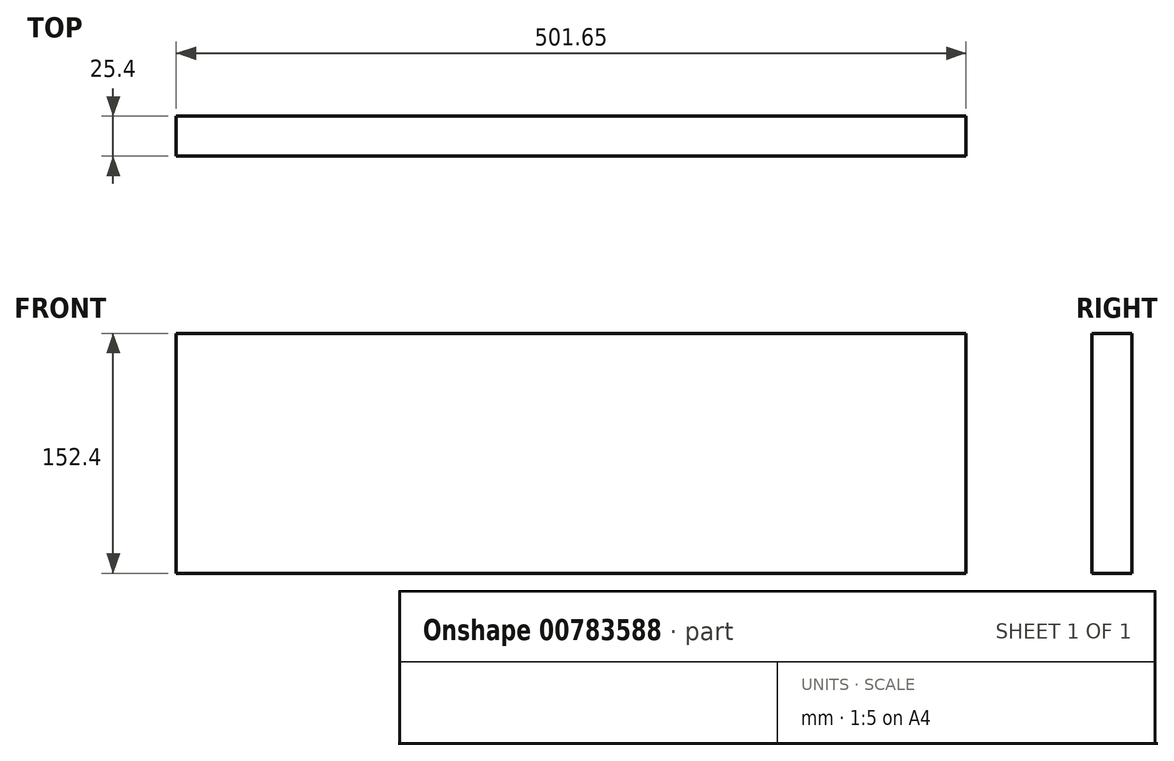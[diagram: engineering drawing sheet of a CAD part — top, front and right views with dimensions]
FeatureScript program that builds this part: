
annotation { "Feature Type Name" : "Feature", "Feature Type Description" : "" }
export const myFeature = defineFeature(function(context is Context, id is Id, definition is map)
    precondition{}
    {
        {
            var Q0;
            Q0=qCreatedBy(makeId("Front.planeOp"),FACE);
            var sketch = newSketch(context, id + "F0", { "sketchPlane" : qUnion([Q0])});
            skLineSegment(sketch, "E0.bottom", {"start": v(0, 0) * mm, "end": v(501.65, 0) * mm});
            skLineSegment(sketch, "E0.top", {"start": v(0, 152.4) * mm, "end": v(501.65, 152.4) * mm});
            skLineSegment(sketch, "E0.left", {"start": v(0, 0) * mm, "end": v(0, 152.4) * mm});
            skLineSegment(sketch, "E0.right", {"start": v(501.65, 0) * mm, "end": v(501.65, 152.4) * mm});
            skSolve(sketch);
        }
        {
            var Q0;
            Q0=makeQuery(id+"F0.imprint","IMPRINT",FACE,{"disambiguationData":[TD([[makeQuery(id+"F0.imprint","IMPRINT",EDGE,{"derivedFrom":sQuery(id+"F0.wireOp",EDGE,"E0.bottom")}),1.0]])]});
            extrude(context, id + "F1", {"entities" : qUnion([Q0]), "depth" : 25.4 * mm, "offsetDistance" : 25.4 * mm});
        }
    });
